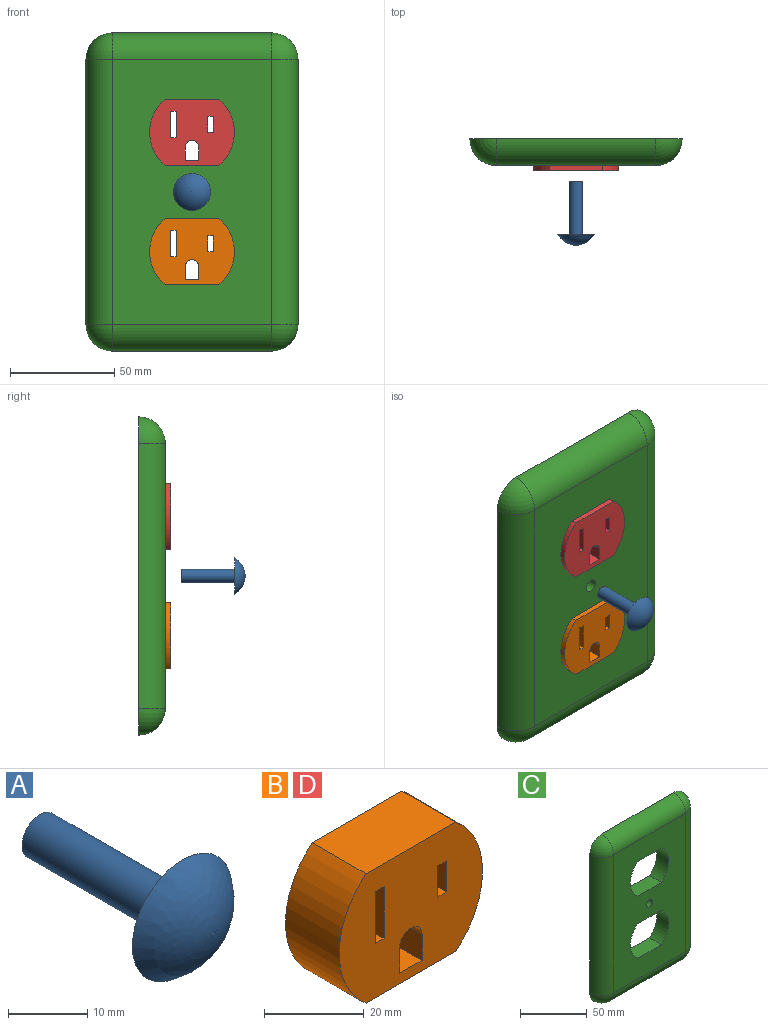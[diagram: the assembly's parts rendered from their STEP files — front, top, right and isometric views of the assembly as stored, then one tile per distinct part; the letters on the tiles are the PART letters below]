
ASSEMBLY  parts=4 mates=3
PART A: 4 faces, bbox 17.8x30.5x17.8 mm
  f0: cylinder r=3.17mm len=25.4mm, axis (0,1,0), area 506.7mm2, adj f1,f2
  f1: plane 6.35x6.35mm, normal (0,1,0), area 31.7mm2, adj f0
  f2: plane 17.78x17.78mm, normal (0,1,0), area 216.6mm2, adj f0,f3
  f3: revolved ~17.78x17.78mm, area 325.3mm2, adj f2
PART B: 18 faces, bbox 40.6x15.2x31.8 mm
  f0: plane 15.24x6.35mm, normal (0,0,1), area 96.8mm2, adj f1,f15,f16,f17
  f1: plane 15.24x6.35mm, normal (1,0,0), area 96.8mm2, adj f0,f2,f16,f17
  f2: cylinder r=3.17mm len=15.24mm, axis (0,1,0), area 152mm2, adj f1,f15,f16,f17
  f3: cylinder r=20.35mm len=31.75mm, axis (0,1,0), area 555.1mm2, adj f4,f12,f16,f17
  f4: plane 25.4x15.24mm, normal (0,0,1), area 387.1mm2, adj f3,f5,f16,f17
  f5: cylinder r=20.35mm len=31.75mm, axis (0,1,0), area 555.1mm2, adj f4,f12,f16,f17
  f6: plane 15.24x7.62mm, normal (-1,0,0), area 116.1mm2, adj f7,f13,f16,f17
  f7: plane 15.24x2.54mm, normal (0,0,1), area 38.7mm2, adj f6,f8,f16,f17
  f8: plane 15.24x7.62mm, normal (1,0,0), area 116.1mm2, adj f7,f13,f16,f17
  f9: plane 15.24x12.7mm, normal (-1,0,0), area 193.5mm2, adj f10,f14,f16,f17
  f10: plane 15.24x2.54mm, normal (0,0,1), area 38.7mm2, adj f9,f11,f16,f17
  f11: plane 15.24x12.7mm, normal (1,0,0), area 193.5mm2, adj f10,f14,f16,f17
  f12: plane 25.4x15.24mm, normal (0,0,-1), area 387.1mm2, adj f3,f5,f16,f17
  f13: plane 15.24x2.54mm, normal (0,0,-1), area 38.7mm2, adj f6,f8,f16,f17
  f14: plane 15.24x2.54mm, normal (0,0,-1), area 38.7mm2, adj f9,f11,f16,f17
  f15: plane 15.24x6.35mm, normal (-1,0,0), area 96.8mm2, adj f0,f2,f16,f17
  f16: plane 40.64x31.75mm, normal (0,-1,0), area 1035.7mm2, adj f0,f1,f2,f3,f4,f5,f6,f7
  f17: plane 40.64x31.75mm, normal (0,1,0), area 1035.7mm2, adj f0,f1,f2,f3,f4,f5,f6,f7
PART C: 40 faces, bbox 101.6x12.7x152.4 mm
  f0: plane 45.72x36.83mm, normal (0,1,0), area 334.6mm2, adj f6,f7,f8,f11,f25,f26,f27,f30
  f1: plane 45.72x36.83mm, normal (0,1,0), area 334.6mm2, adj f3,f4,f5,f10,f22,f23,f24,f29
  f2: plane 11.43x11.43mm, normal (0,1,0), area 70.9mm2, adj f9,f28
  f3: plane 25.4x12.7mm, normal (0,0,1), area 322.6mm2, adj f1,f4,f10,f12
  f4: cylinder r=20.35mm len=31.75mm, axis (0,1,0), area 462.6mm2, adj f1,f3,f5,f12
  f5: plane 25.4x12.7mm, normal (0,0,-1), area 322.6mm2, adj f1,f4,f10,f12
  f6: plane 25.4x12.7mm, normal (0,0,-1), area 322.6mm2, adj f0,f7,f11,f12
  f7: cylinder r=20.35mm len=31.75mm, axis (0,1,0), area 462.6mm2, adj f0,f6,f8,f12
  f8: plane 25.4x12.7mm, normal (0,0,1), area 322.6mm2, adj f0,f7,f11,f12
  f9: cylinder r=3.17mm len=12.7mm, axis (0,1,0), area 253.4mm2, adj f2,f12
  f10: cylinder r=20.35mm len=31.75mm, axis (0,1,0), area 462.6mm2, adj f1,f3,f5,f12
  f11: cylinder r=20.35mm len=31.75mm, axis (0,1,0), area 462.6mm2, adj f0,f6,f8,f12
  f12: plane 127x76.2mm, normal (0,-1,0), area 7358.9mm2, adj f3,f4,f5,f6,f7,f8,f9,f10
  f13: plane 152.4x101.6mm, normal (0,1,0), area 1214.7mm2, adj f14,f15,f16,f17,f18,f19,f20,f21
  f14: sphere r=12.7mm, area 253.4mm2, adj f13,f15,f16
  f15: cylinder r=12.7mm len=127mm, axis (0,0,1), area 2533.5mm2, adj f12,f13,f14,f17
  f16: cylinder r=12.7mm len=76.2mm, axis (1,0,0), area 1520.1mm2, adj f12,f13,f14,f18
  f17: sphere r=12.7mm, area 253.4mm2, adj f13,f15,f19
  f18: sphere r=12.7mm, area 253.4mm2, adj f13,f16,f20
  f19: cylinder r=12.7mm len=76.2mm, axis (-1,0,0), area 1520.1mm2, adj f12,f13,f17,f21
  f20: cylinder r=12.7mm len=127mm, axis (0,0,-1), area 2533.5mm2, adj f12,f13,f18,f21
  f21: sphere r=12.7mm, area 253.4mm2, adj f13,f19,f20
  f22: plane 27.13x10.16mm, normal (0,0,-1), area 275.6mm2, adj f1,f23,f29,f31
  f23: cylinder r=22.89mm len=36.83mm, axis (0,1,0), area 434.8mm2, adj f1,f22,f24,f31
  f24: plane 27.13x10.16mm, normal (0,0,1), area 275.6mm2, adj f1,f23,f29,f31
  f25: plane 27.13x10.16mm, normal (0,0,1), area 275.6mm2, adj f0,f26,f30,f31
  f26: cylinder r=22.89mm len=36.83mm, axis (0,1,0), area 434.8mm2, adj f0,f25,f27,f31
  f27: plane 27.13x10.16mm, normal (0,0,-1), area 275.6mm2, adj f0,f26,f30,f31
  f28: cylinder r=5.71mm len=11.43mm, axis (0,1,0), area 364.8mm2, adj f2,f31
  f29: cylinder r=22.89mm len=36.83mm, axis (0,1,0), area 434.8mm2, adj f1,f22,f24,f31
  f30: cylinder r=22.89mm len=36.83mm, axis (0,1,0), area 434.8mm2, adj f0,f25,f27,f31
  f31: plane 127x76.2mm, normal (0,1,0), area 6618.6mm2, adj f22,f23,f24,f25,f26,f27,f28,f29
  f32: sphere r=10.16mm, area 162.1mm2, adj f13,f33,f34
  f33: cylinder r=10.16mm len=127mm, axis (0,0,1), area 2026.8mm2, adj f13,f31,f32,f35
  f34: cylinder r=10.16mm len=76.2mm, axis (1,0,0), area 1216.1mm2, adj f13,f31,f32,f36
  f35: sphere r=10.16mm, area 162.1mm2, adj f13,f33,f37
  f36: sphere r=10.16mm, area 162.1mm2, adj f13,f34,f38
  f37: cylinder r=10.16mm len=76.2mm, axis (-1,0,0), area 1216.1mm2, adj f13,f31,f35,f39
  f38: cylinder r=10.16mm len=127mm, axis (0,0,-1), area 2026.8mm2, adj f13,f31,f36,f39
  f39: sphere r=10.16mm, area 162.1mm2, adj f13,f37,f38
PART D: same geometry as B
PLACE A t=(-4.75,-26.8,-6.13)mm
PLACE B t=(-4.75,-6.35,-34.7)mm
PLACE C t=(-4.75,-6.35,-6.13)mm fixed
PLACE D t=(-4.75,-6.35,22.45)mm
MATE slider C.f9 <-> A.f0  axis (0,1,0) through (-4.75,-12.7,-6.13)mm
MATE fastened B.f17 <-> C.f0  axis (0,1,0) through (-4.75,-6.35,-18.83)mm
MATE fastened D.f17 <-> C.f1  axis (0,1,0) through (-4.75,-6.35,38.32)mm
